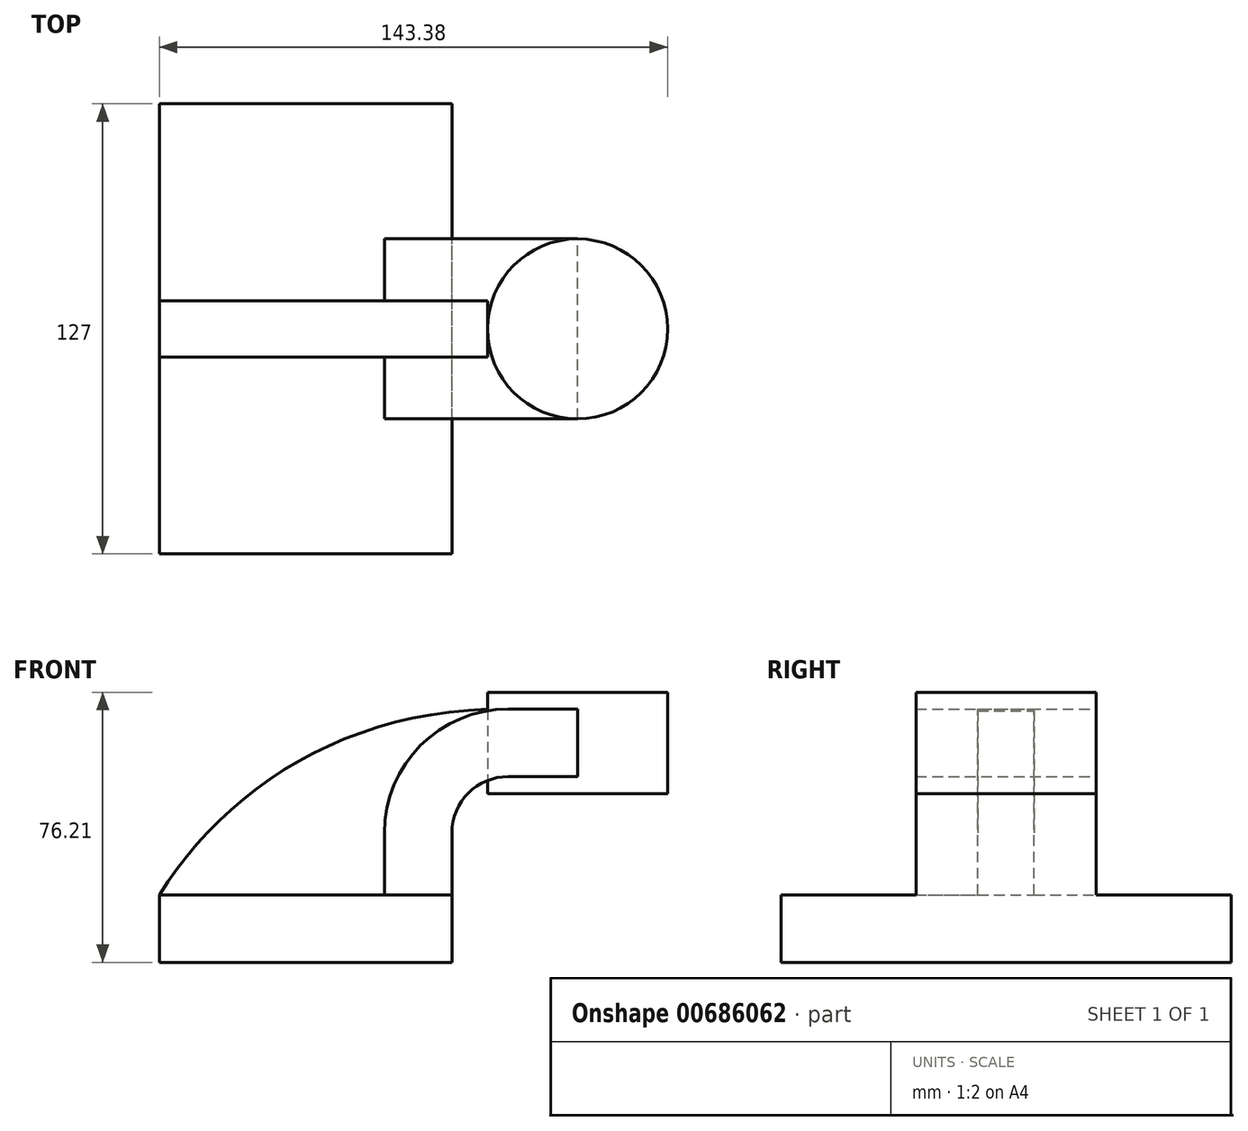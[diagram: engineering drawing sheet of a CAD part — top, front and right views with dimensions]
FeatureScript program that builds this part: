
annotation { "Feature Type Name" : "Feature", "Feature Type Description" : "" }
export const myFeature = defineFeature(function(context is Context, id is Id, definition is map)
    precondition{}
    {
        {
            var Q0;
            Q0=qCreatedBy(makeId("Front.planeOp"),FACE);
            var sketch = newSketch(context, id + "F0", { "sketchPlane" : qUnion([Q0])});
            skLineSegment(sketch, "E0.bottom", {"start": v(-41.28, 9.52) * mm, "end": v(41.28, 9.53) * mm});
            skLineSegment(sketch, "E0.top", {"start": v(-41.28, -9.53) * mm, "end": v(41.28, -9.53) * mm});
            skLineSegment(sketch, "E0.left", {"start": v(-41.28, 9.52) * mm, "end": v(-41.28, -9.53) * mm});
            skLineSegment(sketch, "E0.right", {"start": v(41.28, 9.53) * mm, "end": v(41.28, -9.52) * mm});
            skPoint(sketch, "E0.middle", {"position": v(0, 0) * mm});
            skLineSegment(sketch, "E1.bottom", {"start": v(102.1, 38.1) * mm, "end": v(51.3, 38.1) * mm});
            skLineSegment(sketch, "E1.top", {"start": v(102.1, 66.68) * mm, "end": v(51.3, 66.68) * mm});
            skLineSegment(sketch, "E1.left", {"start": v(102.1, 38.1) * mm, "end": v(102.1, 66.68) * mm});
            skLineSegment(sketch, "E1.right", {"start": v(51.3, 38.1) * mm, "end": v(51.3, 66.68) * mm});
            skPoint(sketch, "E1.middle", {"position": v(76.7, 52.39) * mm});
            skLineSegment(sketch, "E2", {"start": v(41.27, 9.53) * mm, "end": v(41.27, 27) * mm});
            skArc(sketch, "E3", {"start": v(41.27, 27) * mm, "mid": v(45.92, 38.23) * mm, "end": v(57.15, 42.88) * mm});
            skLineSegment(sketch, "E4", {"start": v(57.15, 42.88) * mm, "end": v(76.7, 42.88) * mm});
            skLineSegment(sketch, "E5.0", {"start": v(57.15, 61.93) * mm, "end": v(76.7, 61.93) * mm});
            skArc(sketch, "E5.1", {"start": v(22.22, 27) * mm, "mid": v(32.45, 51.7) * mm, "end": v(57.15, 61.93) * mm});
            skLineSegment(sketch, "E5.2", {"start": v(22.22, 9.53) * mm, "end": v(22.22, 27) * mm});
            skLineSegment(sketch, "E6", {"start": v(76.7, 38.1) * mm, "end": v(76.7, 66.68) * mm});
            skFitSpline(sketch, "E7", {"points": [v(-41.28, 9.53) * mm, v(57.15, 61.93) * mm], "startDerivative": vector(56.03, 89.87) * mm, "endDerivative": vector(135.14, -2.07) * mm});
            skSolve(sketch);
        }
        {
            var Q0;
            Q0=makeQuery(id+"F0.imprint","IMPRINT",FACE,{"disambiguationData":[TD([[makeQuery(id+"F0.imprint","IMPRINT",EDGE,{"derivedFrom":sQuery(id+"F0.wireOp",EDGE,"E0.top")}),1.0]])]});
            extrude(context, id + "F1", {"entities" : qUnion([Q0]), "endBound" : BoundingType.SYMMETRIC, "depth" : 127 * mm, "offsetDistance" : 25.4 * mm});
        }
        {
            var Q0;
            {var subQ1=sQuery(id+"F0.wireOp",EDGE,"E2");Q0=makeQuery(id+"F0.imprint","IMPRINT",FACE,{"disambiguationData":[TD([[makeQuery(id+"F0.imprint","IMPRINT",EDGE,{"derivedFrom":subQ1}),1.0]])]});}
            extrude(context, id + "F2", {"entities" : qUnion([Q0]), "operationType" : NewBodyOperationType.ADD, "endBound" : BoundingType.SYMMETRIC, "depth" : 50.8 * mm, "offsetDistance" : 25.4 * mm});
        }
        {
            var Q0;
            {var subQ1=sQuery(id+"F0.wireOp",EDGE,"E4");Q0=makeQuery(id+"F0.imprint","IMPRINT",FACE,{"disambiguationData":[TD([[makeQuery(id+"F0.imprint","IMPRINT",EDGE,{"derivedFrom":subQ1}),1.0]])]});}
            extrude(context, id + "F3", {"entities" : qUnion([Q0]), "operationType" : NewBodyOperationType.ADD, "endBound" : BoundingType.SYMMETRIC, "depth" : 50.8 * mm, "offsetDistance" : 25.4 * mm});
        }
        {
            var Q0;
            {var subQ0=sQuery(id+"F0.wireOp",EDGE,"E5.2");Q0=makeQuery(id+"F0.imprint","IMPRINT",FACE,{"disambiguationData":[TD([[makeQuery(id+"F0.imprint","IMPRINT",EDGE,{"derivedFrom":subQ0}),1.0]])]});}
            extrude(context, id + "F4", {"entities" : qUnion([Q0]), "operationType" : NewBodyOperationType.ADD, "endBound" : BoundingType.SYMMETRIC, "depth" : 15.88 * mm, "offsetDistance" : 25.4 * mm});
        }
        {
            var Q0;
            {var subQ0=sQuery(id+"F0.wireOp",EDGE,"E1.left");Q0=makeQuery(id+"F0.imprint","IMPRINT",FACE,{"disambiguationData":[TD([[makeQuery(id+"F0.imprint","IMPRINT",EDGE,{"derivedFrom":subQ0}),1.0]])]});}
            var Q1;
            Q1=sQuery(id+"F0.wireOp",EDGE,"E6");
            revolve(context, id + "F5", {"entities" : qUnion([Q0]), "axis" : qUnion([Q1]), "revolveType" : RevolveType.FULL});
        }
    });
